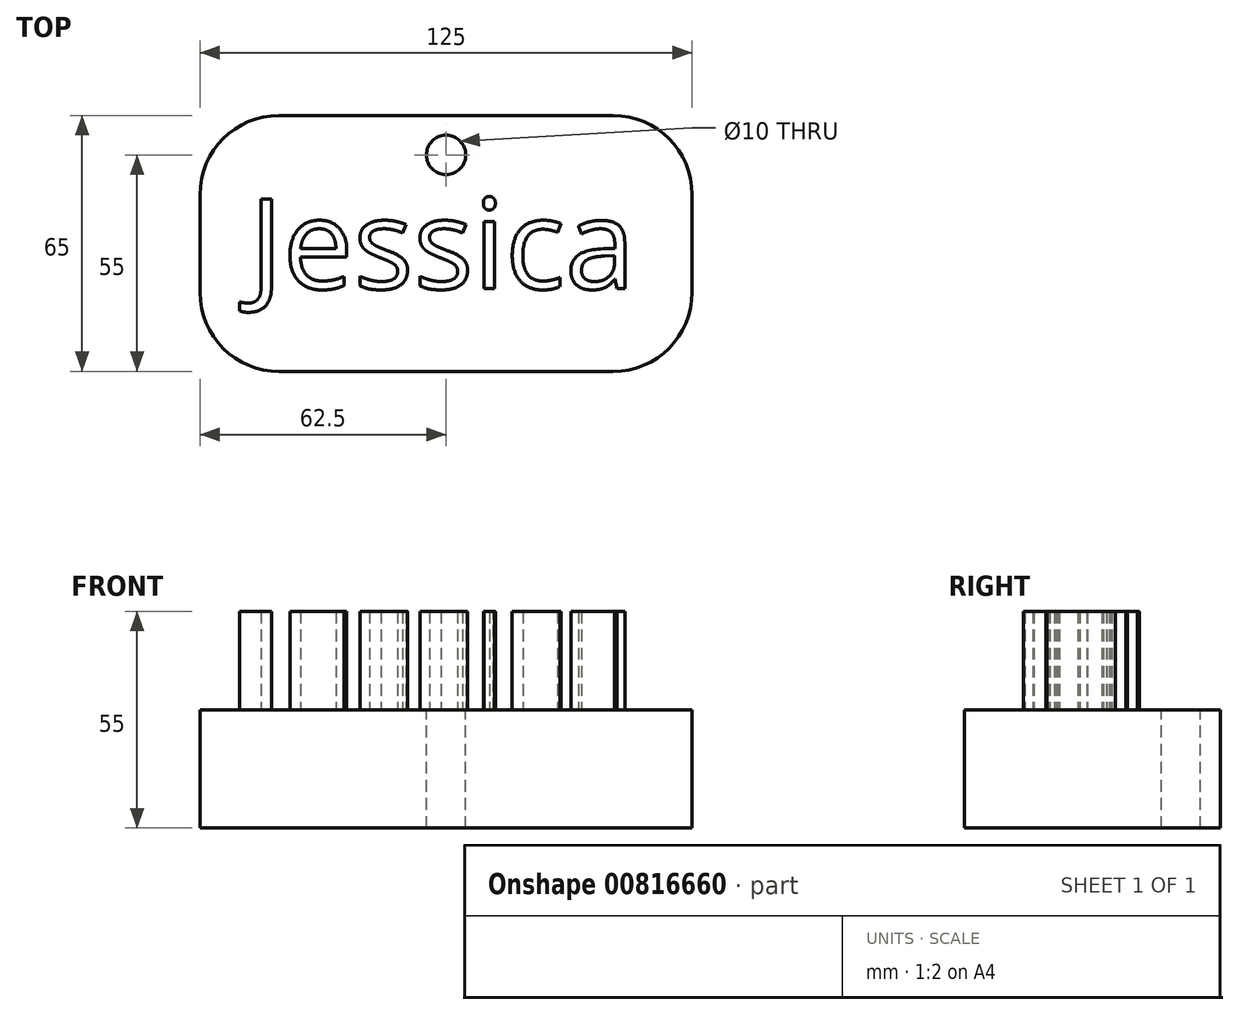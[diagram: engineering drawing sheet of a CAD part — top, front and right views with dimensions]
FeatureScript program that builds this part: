
annotation { "Feature Type Name" : "Feature", "Feature Type Description" : "" }
export const myFeature = defineFeature(function(context is Context, id is Id, definition is map)
    precondition{}
    {
        {
            var Q0;
            Q0=qCreatedBy(makeId("Top.planeOp"),FACE);
            var sketch = newSketch(context, id + "F0", { "sketchPlane" : qUnion([Q0])});
            skLineSegment(sketch, "E0.bottom", {"start": v(62.5, 32.5) * mm, "end": v(-62.5, 32.5) * mm});
            skLineSegment(sketch, "E0.top", {"start": v(62.5, -32.5) * mm, "end": v(-62.5, -32.5) * mm});
            skLineSegment(sketch, "E0.left", {"start": v(62.5, 32.5) * mm, "end": v(62.5, -32.5) * mm});
            skLineSegment(sketch, "E0.right", {"start": v(-62.5, 32.5) * mm, "end": v(-62.5, -32.5) * mm});
            skPoint(sketch, "E0.middle", {"position": v(0, 0) * mm});
            skSolve(sketch);
        }
        {
            var Q0;
            Q0 = qSketchRegion(id + "F0", true);
            extrude(context, id + "F1", {"entities" : qUnion([Q0]), "depth" : 30 * mm, "offsetDistance" : 25 * mm});
        }
        {
            var Q0;
            Q0=makeQuery(id+"F1.opExtrude","CAP_FACE",FACE,{"disambiguationData":[OSD([sQuery(id+"F0.wireOp",EDGE,"E0.bottom"),sQuery(id+"F0.wireOp",EDGE,"E0.top"),sQuery(id+"F0.wireOp",EDGE,"E0.left"),sQuery(id+"F0.wireOp",EDGE,"E0.right")])],"isStart":false});
            var sketch = newSketch(context, id + "F2", { "sketchPlane" : qUnion([Q0])});
            skText(sketch, "E1", { "text": "Jessica\n", "fontName": "OpenSans-Regular.ttf"});
            skLineSegment(sketch, "E2", {"start": v(0, 11.5) * mm, "end": v(0, 32.5) * mm, "construction": true});
            skPoint(sketch, "E2.endSnap0", {"position": v(0, 11.5) * mm});
            skLineSegment(sketch, "E3", {"start": v(0, -11.5) * mm, "end": v(0, -32.5) * mm, "construction": true});
            skLineSegment(sketch, "E4", {"start": v(50, 0) * mm, "end": v(62.5, 0) * mm, "construction": true});
            skLineSegment(sketch, "E5", {"start": v(-50, 0) * mm, "end": v(-62.5, 0) * mm, "construction": true});
            skPoint(sketch, "E5.endSnap0", {"position": v(-50, 0) * mm});
            const initialGuessF2  = {"E1": [-0.05, -0.0115, 1, 0, 0.023]};
            skSetInitialGuess(sketch, initialGuessF2);
            skSolve(sketch);
        }
        {
            var Q0;
            Q0 = qSketchRegion(id + "F2", true);
            extrude(context, id + "F3", {"entities" : qUnion([Q0]), "operationType" : NewBodyOperationType.ADD, "depth" : 25 * mm, "offsetDistance" : 25 * mm});
        }
        {
            var Q0;
            {var subQ0=sQuery(id+"F0.wireOp",EDGE,"E0.top");var subQ1=sQuery(id+"F0.wireOp",EDGE,"E0.right");var subQ2=sQuery(id+"F0.wireOp",EDGE,"E0.bottom");var subQ3=sQuery(id+"F0.wireOp",EDGE,"E0.left");Q0=makeQuery(id+"F3.boolean.opBoolean","SPLIT",FACE,{"disambiguationData":[TD([makeQuery(id+"F1.opExtrude","SWEPT_FACE",FACE,{"disambiguationData":[OSD([subQ2])]})])],"derivedFrom":makeQuery(id+"F1.opExtrude","CAP_FACE",FACE,{"disambiguationData":[OSD([subQ2,subQ0,subQ3,subQ1])],"isStart":false})});}
            var sketch = newSketch(context, id + "F4", { "sketchPlane" : qUnion([Q0])});
            skLineSegment(sketch, "E6", {"start": v(0, 32.5) * mm, "end": v(0, 22.5) * mm});
            skCircle(sketch, "E7", {"center": v(0, 22.5) * mm, "radius": 5 * mm});
            skSolve(sketch);
        }
        {
            var Q0;
            Q0=makeQuery(id+"F4.imprint","IMPRINT",FACE,{"disambiguationData":[TD([[makeQuery(id+"F4.imprint","IMPRINT",EDGE,{"derivedFrom":sQuery(id+"F4.wireOp",EDGE,"E7")}),1.0]])]});
            extrude(context, id + "F5", {"entities" : qUnion([Q0]), "operationType" : NewBodyOperationType.REMOVE, "oppositeDirection" : true, "depth" : 51.3 * mm, "offsetDistance" : 25 * mm});
        }
        {
            var Q0;
            Q0=makeQuery(id+"F1.opExtrude","SWEPT_EDGE",EDGE,{"disambiguationData":[OSD([sQuery(id+"F0.wireOp",EDGE,"E0.bottom"),sQuery(id+"F0.wireOp",EDGE,"E0.left")])]});
            var Q1;
            Q1=makeQuery(id+"F1.opExtrude","SWEPT_EDGE",EDGE,{"disambiguationData":[OSD([sQuery(id+"F0.wireOp",EDGE,"E0.top"),sQuery(id+"F0.wireOp",EDGE,"E0.left")])]});
            var Q2;
            Q2=makeQuery(id+"F1.opExtrude","SWEPT_EDGE",EDGE,{"disambiguationData":[OSD([sQuery(id+"F0.wireOp",EDGE,"E0.bottom"),sQuery(id+"F0.wireOp",EDGE,"E0.right")])]});
            var Q3;
            Q3=makeQuery(id+"F1.opExtrude","SWEPT_EDGE",EDGE,{"disambiguationData":[OSD([sQuery(id+"F0.wireOp",EDGE,"E0.top"),sQuery(id+"F0.wireOp",EDGE,"E0.right")])]});
            fillet(context, id + "F6", {"entities" : qUnion([Q0, Q1, Q2, Q3]), "radius" : 20.04 * mm, "tangentPropagation" : true, "allowEdgeOverflow" : false});
        }
    });
